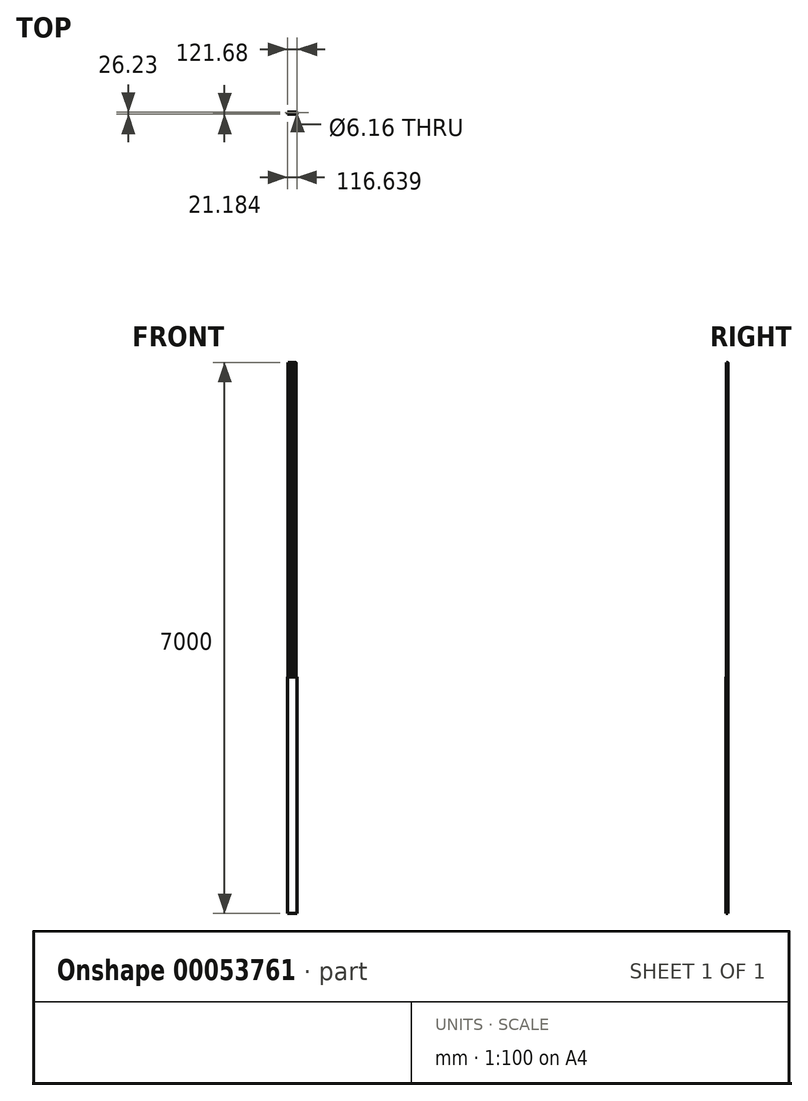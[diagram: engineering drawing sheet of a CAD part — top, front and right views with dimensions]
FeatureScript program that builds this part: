
annotation { "Feature Type Name" : "Feature", "Feature Type Description" : "" }
export const myFeature = defineFeature(function(context is Context, id is Id, definition is map)
    precondition{}
    {
        {
            var Q0;
            Q0=qCreatedBy(makeId("Top.planeOp"),FACE);
            var sketch = newSketch(context, id + "F0", { "sketchPlane" : qUnion([Q0])});
            skText(sketch, "E0", { "text": "Makerfaire", "fontName": "OpenSans-BoldItalic.ttf"});
            const initialGuessF0  = {"E0": [-0.02874, 0.03491, 1, 0, 0.01347]};
            skSetInitialGuess(sketch, initialGuessF0);
            skSolve(sketch);
        }
        {
            var Q0;
            Q0=qCreatedBy(makeId("Top.planeOp"),FACE);
            var sketch = newSketch(context, id + "F1", { "sketchPlane" : qUnion([Q0])});
            skLineSegment(sketch, "E1.bottom", {"start": v(-34.5, 53.98) * mm, "end": v(87.17, 53.98) * mm});
            skLineSegment(sketch, "E1.top", {"start": v(-34.5, 27.75) * mm, "end": v(87.17, 27.75) * mm});
            skLineSegment(sketch, "E1.left", {"start": v(-34.5, 53.98) * mm, "end": v(-34.5, 27.75) * mm});
            skLineSegment(sketch, "E1.right", {"start": v(87.17, 53.98) * mm, "end": v(87.17, 27.75) * mm});
            skCircle(sketch, "E2", {"center": v(82.13, 48.93) * mm, "radius": 3.08 * mm});
            skSolve(sketch);
        }
        {
            var Q0;
            Q0 = qSketchRegion(id + "F1", true);
            var Q1;
            Q1=makeQuery(id+"F1.imprint","IMPRINT",FACE,{"disambiguationData":[TD([[makeQuery(id+"F1.imprint","IMPRINT",EDGE,{"derivedFrom":sQuery(id+"F1.wireOp",EDGE,"E1.bottom")}),-1.0]])]});
            extrude(context, id + "F2", {"entities" : qUnion([Q0, Q1]), "depth" : 3000 * mm});
        }
        {
            var Q0;
            Q0 = qSketchRegion(id + "F0", true);
            extrude(context, id + "F3", {"entities" : qUnion([Q0]), "operationType" : NewBodyOperationType.ADD, "depth" : 7000 * mm});
        }
    });
